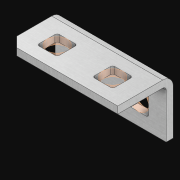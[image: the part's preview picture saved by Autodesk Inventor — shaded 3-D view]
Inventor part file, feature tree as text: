
AUTODESK INVENTOR PART (.ipt)
format: ipt  version: 2021 (Build 250183000, 183)  size: 533,504 bytes
history: native  units: in
note: dims shown in document units (in); Inventor stores cm internally (conversion verified against a paired STEP export)
features: extrude x5, other x4, sketch x3, pattern_linear x1, sheet_metal_op x1
ambient origin geometry x8: Origin, YZ Plane, XZ Plane, XY Plane, X Axis, Y Axis, Z Axis, Center Point
bodies: Solid1 (feature_tree)
feature tree (14):
  pattern_linear  "Rectangular Pattern1"  Spacing1=0.063in  [1 undecoded]
  extrude  "Extrusion1"  Depth=0.5in
  sketch  "Sketch1"  dims[d0=0.182in]
  other  "Srf1"
  sketch  "Sketch2"  dims[d1=0.063in d2=0.0in]
  other  "Srf2"
  other  "Srf3"
  other  "Srf4"
  sketch  "Sketch3"  dims[d3=0.182in d4=0.063in d5=0.0in d8=0.5in d9=16.5in d10=0.0in]
  sheet_metal_op  "Fold1"
  extrude  "ExtrusionSrf1"  Depth=0.5in TaperAngle=0.0deg
  extrude  "ExtrusionSrf2"  [1 undecoded]
  extrude  "ExtrusionSrf3"  [1 undecoded]
  extrude  "ExtrusionSrf37"  [1 undecoded]
note: 4 required parameter values undecoded (feature->parameter linkage not recoverable at this tier; creation-order binding heuristic only, values carry confidence <= 0.55)
